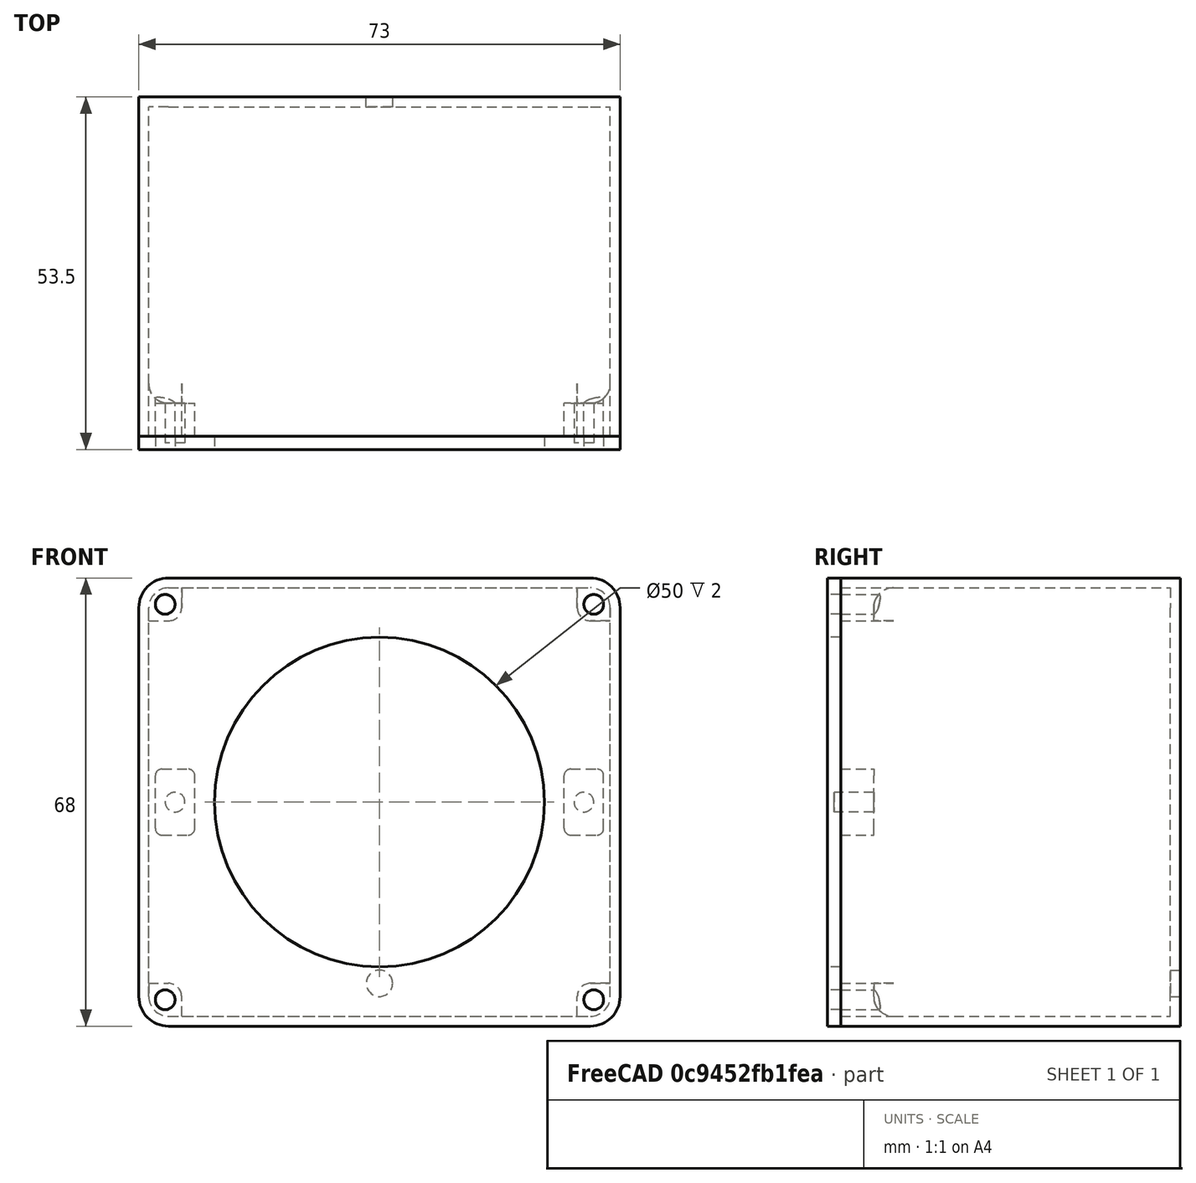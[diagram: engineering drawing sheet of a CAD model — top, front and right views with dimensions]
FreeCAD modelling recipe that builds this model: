
FCSTD DOCUMENT  (FreeCAD 0.19R24291 (Git))
Label: mini-speaker-enclosure
License: All rights reserved
LicenseURL: http://en.wikipedia.org/wiki/All_rights_reserved
objects: Part::Cut×15, Part::Cylinder×15, Part::Fillet×10, Part::Box×9, Part::Fuse×7, Part::Refine×2
note: 58 computed .brp shape members not serialized (recipe doc carries the construction recipe); baked Part::Feature solids carry a one-line shape summary decoded from their .brp

FEATURE [Part::Box] Box  label="Cube"
  AttacherType = Attacher::AttachEngine3D
  Height = 65
  Length = 70
  Width = 50
FEATURE [Part::Box] Box001  label="Cube001"
  AttacherType = Attacher::AttachEngine3D
  Height = 68
  Length = 73
  Placement = pos=(-1.5,0,-1.5) rot=(0,0,1;0rad)
  Width = 51.5
FEATURE [Part::Cut] Cut
  Base = -> Box001
  Tool = -> Box
FEATURE [Part::Fillet] Fillet
  Base = -> Cut
  Edges = 4 edges r=3: [Edge17,Edge19,Edge21,Edge22]
FEATURE [Part::Fillet] Fillet001
  Base = -> Fillet
  Edges = 4 edges r=4.5: [Edge29,Edge31,Edge32,Edge34]
FEATURE [Part::Box] Box002  label="Cube002"
  AttacherType = Attacher::AttachEngine3D
  Height = 5
  Length = 5
  Width = 5
FEATURE [Part::Cylinder] Cylinder
  Angle = 360
  AttacherType = Attacher::AttachEngine3D
  Height = 10
  Placement = pos=(2.5,1e-15,2.5) rot=(-1,0,0;1.5708rad)
  Radius = 1.5
FEATURE [Part::Box] Box003  label="Cube003"
  AttacherType = Attacher::AttachEngine3D
  Height = 5
  Length = 5
  Placement = pos=(65,0,0) rot=(0,0,1;0rad)
  Width = 5
FEATURE [Part::Cylinder] Cylinder001
  Angle = 360
  AttacherType = Attacher::AttachEngine3D
  Height = 10
  Placement = pos=(67.5,1e-15,2.5) rot=(-1,0,0;1.5708rad)
  Radius = 1.5
FEATURE [Part::Box] Box004  label="Cube004"
  AttacherType = Attacher::AttachEngine3D
  Height = 5
  Length = 5
  Placement = pos=(0,0,60) rot=(0,0,1;0rad)
  Width = 5
FEATURE [Part::Cylinder] Cylinder002
  Angle = 360
  AttacherType = Attacher::AttachEngine3D
  Height = 10
  Placement = pos=(2.5,-1.2e-14,62.5) rot=(-1,0,0;1.5708rad)
  Radius = 1.5
FEATURE [Part::Cylinder] Cylinder003
  Angle = 360
  AttacherType = Attacher::AttachEngine3D
  Height = 10
  Placement = pos=(67.5,-1.2e-14,62.5) rot=(-1,0,0;1.5708rad)
  Radius = 1.5
FEATURE [Part::Box] Box005  label="Cube005"
  AttacherType = Attacher::AttachEngine3D
  Height = 5
  Length = 5
  Placement = pos=(65,0,60) rot=(0,0,1;0rad)
  Width = 5
FEATURE [Part::Fuse] Fusion
  Base = -> Fillet001
  Tool = -> Box005
FEATURE [Part::Fuse] Fusion001
  Base = -> Fusion
  Tool = -> Box004
FEATURE [Part::Fuse] Fusion002
  Base = -> Fusion001
  Tool = -> Box003
FEATURE [Part::Fuse] Fusion003
  Base = -> Fusion002
  Tool = -> Box002
FEATURE [Part::Fillet] Fillet002
  Base = -> Fusion003
  Edges = 2 edges r=3: [Edge76,Edge83]
FEATURE [Part::Fillet] Fillet003
  Base = -> Fillet002
  Edges = 1 edges r=2: [Edge23]
FEATURE [Part::Cut] Cut001
  Base = -> Fillet003
  Tool = -> Cylinder
FEATURE [Part::Fillet] Fillet004
  Base = -> Cut001
  Edges = 2 edges r=3: [Edge98,Edge111]
FEATURE [Part::Fillet] Fillet005
  Base = -> Fillet004
  Edges = 1 edges r=2: [Edge23]
FEATURE [Part::Cut] Cut002
  Base = -> Fillet005
  Tool = -> Cylinder002
FEATURE [Part::Fillet] Fillet006
  Base = -> Cut002
  Edges = 4 edges r=3: [Edge18,Edge69,Edge95,Edge105]
FEATURE [Part::Fillet] Fillet007
  Base = -> Fillet006
  Edges = 2 edges r=2: [Edge24,Edge133]
FEATURE [Part::Cut] Cut003
  Base = -> Fillet007
  Tool = -> Cylinder001
FEATURE [Part::Cut] Cut004
  Base = -> Cut003
  Tool = -> Cylinder003
FEATURE [Part::Refine] Cut004001
  Source = -> Cut004
FEATURE [Part::Cylinder] Cylinder004
  Angle = 360
  AttacherType = Attacher::AttachEngine3D
  Height = 60
  Placement = pos=(35,5,5) rot=(-1,0,0;1.5708rad)
  Radius = 2
FEATURE [Part::Cut] Cut004002  label="Back"
  Base = -> Cut004001
  Tool = -> Cylinder004
FEATURE [Part::Box] Box006  label="Cube006"
  AttacherType = Attacher::AttachEngine3D
  Height = 68
  Length = 73
  Placement = pos=(-1.5,-1,-1.5) rot=(0,0,1;0rad)
  Width = 2
FEATURE [Part::Fillet] Fillet008
  Base = -> Box006
  Edges = 4 edges r=4.5: [Edge2,Edge4,Edge6,Edge8]
FEATURE [Part::Cylinder] Cylinder005
  Angle = 360
  AttacherType = Attacher::AttachEngine3D
  Height = 10
  Placement = pos=(35,0,32.5) rot=(1,0,0;1.5708rad)
  Radius = 25.5
FEATURE [Part::Cut] Cut004003
  Base = -> Fillet008
  Tool = -> Cylinder005
FEATURE [Part::Cylinder] Cylinder006
  Angle = 360
  AttacherType = Attacher::AttachEngine3D
  Height = 10
  Placement = pos=(35,4,32.5) rot=(1,0,0;1.5708rad)
  Radius = 27.5
FEATURE [Part::Box] Box007  label="Cube007"
  AttacherType = Attacher::AttachEngine3D
  Height = 10
  Length = 6
  Placement = pos=(1,1,27.5) rot=(0,0,1;0rad)
  Width = 5
FEATURE [Part::Box] Box008  label="Cube008"
  AttacherType = Attacher::AttachEngine3D
  Height = 10
  Length = 6
  Placement = pos=(63,1,27.5) rot=(0,0,1;0rad)
  Width = 5
FEATURE [Part::Cut] Cut004004
  Base = -> Cut004003
  Tool = -> Cylinder006
FEATURE [Part::Fuse] Fusion004
  Base = -> Cut004004
  Tool = -> Box007
FEATURE [Part::Fuse] Fusion005
  Base = -> Fusion004
  Placement = pos=(0,-53.5,0) rot=(0,0,1;0rad)
  Tool = -> Box008
FEATURE [Part::Cylinder] Cylinder008
  Angle = 360
  AttacherType = Attacher::AttachEngine3D
  Height = 10
  Placement = pos=(4,-43.5,32.5) rot=(1,0,0;1.5708rad)
  Radius = 1.5
FEATURE [Part::Cylinder] Cylinder009
  Angle = 360
  AttacherType = Attacher::AttachEngine3D
  Height = 10
  Placement = pos=(66,-43.5,32.5) rot=(1,0,0;1.5708rad)
  Radius = 1.5
FEATURE [Part::Cut] Cut004005
  Base = -> Fusion005
  Tool = -> Cylinder008
FEATURE [Part::Cut] Cut004006  label="Front"
  Base = -> Cut004005
  Placement = pos=(0,46,0) rot=(0,0,1;0rad)
  Tool = -> Cylinder009
FEATURE [Part::Cylinder] Cylinder010
  Angle = 360
  AttacherType = Attacher::AttachEngine3D
  Height = 10
  Placement = pos=(2.5,4e-16,2.5) rot=(1,0,0;1.5708rad)
  Radius = 1.5
FEATURE [Part::Cylinder] Cylinder011
  Angle = 360
  AttacherType = Attacher::AttachEngine3D
  Height = 10
  Placement = pos=(67.5,0,2.5) rot=(1,0,0;1.5708rad)
  Radius = 1.5
FEATURE [Part::Cylinder] Cylinder012
  Angle = 360
  AttacherType = Attacher::AttachEngine3D
  Height = 10
  Placement = pos=(67.5,1.33e-14,62.5) rot=(1,0,0;1.5708rad)
  Radius = 1.5
FEATURE [Part::Cylinder] Cylinder013
  Angle = 360
  AttacherType = Attacher::AttachEngine3D
  Height = 10
  Placement = pos=(2.5,1.3e-14,62.5) rot=(1,0,0;1.5708rad)
  Radius = 1.5
FEATURE [Part::Cut] Cut004007
  Base = -> Cut004006
  Tool = -> Cylinder010
FEATURE [Part::Cut] Cut004008
  Base = -> Cut004007
  Tool = -> Cylinder011
FEATURE [Part::Cut] Cut004009
  Base = -> Cut004008
  Tool = -> Cylinder012
FEATURE [Part::Cut] Cut004010
  Base = -> Cut004009
  Placement = pos=(0,6.5,0) rot=(0,0,1;0rad)
  Tool = -> Cylinder013
FEATURE [Part::Cylinder] Cylinder014
  Angle = 360
  AttacherType = Attacher::AttachEngine3D
  Height = 2
  Placement = pos=(35,7.2e-15,32.5) rot=(1,0,0;1.5708rad)
  Radius = 25
FEATURE [Part::Cylinder] Cylinder015
  Angle = 360
  AttacherType = Attacher::AttachEngine3D
  Height = 2
  Placement = pos=(35,0,32.5) rot=(1,0,0;1.5708rad)
  Radius = 28.5
FEATURE [Part::Fuse] Fusion006
  Base = -> Cut004010
  Tool = -> Cylinder015
FEATURE [Part::Cut] Cut004011
  Base = -> Fusion006
  Tool = -> Cylinder014
FEATURE [Part::Refine] Cut004011001  label="Front001"
  Source = -> Cut004011
FEATURE [Part::Fillet] Fillet009
  Base = -> Cut004011001
  Edges = 8 edges r=1: [Edge48,Edge50,Edge52,Edge53,Edge59,Edge61,Edge63,Edge65]
